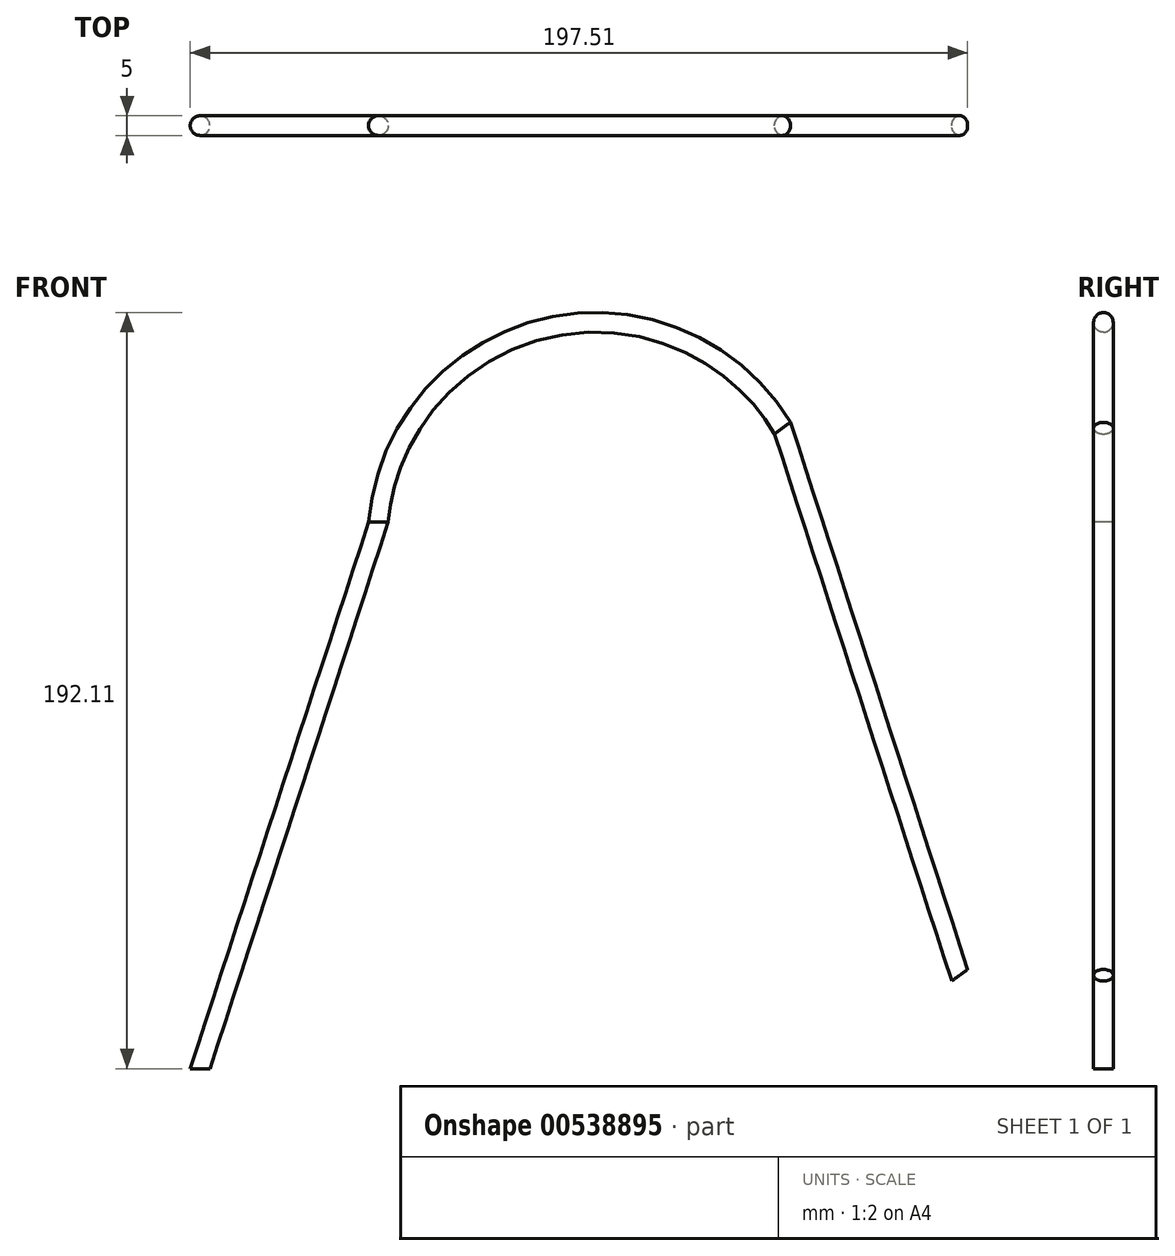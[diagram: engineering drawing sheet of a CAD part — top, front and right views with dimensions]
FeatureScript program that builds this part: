
annotation { "Feature Type Name" : "Feature", "Feature Type Description" : "" }
export const myFeature = defineFeature(function(context is Context, id is Id, definition is map)
    precondition{}
    {
        {
            var Q0;
            Q0=qCreatedBy(makeId("Front.planeOp"),FACE);
            var sketch = newSketch(context, id + "F0", { "sketchPlane" : qUnion([Q0])});
            skLineSegment(sketch, "E0", {"start": v(-60, 0) * mm, "end": v(-15, 137.84) * mm});
            skLineSegment(sketch, "E1", {"start": v(15, 139.03) * mm, "end": v(60, 0) * mm});
            skLineSegment(sketch, "E2", {"start": v(0, 0) * mm, "end": v(0, 168.43) * mm, "construction": true});
            skArc(sketch, "E3", {"start": v(15, 139.03) * mm, "mid": v(-0.45, 149.8) * mm, "end": v(-15, 137.84) * mm});
            skSolve(sketch);
        }
        {
            var Q0;
            Q0=qCreatedBy(makeId("Top.planeOp"),FACE);
            var sketch = newSketch(context, id + "F1", { "sketchPlane" : qUnion([Q0])});
            skCircle(sketch, "E4", {"center": v(-100.35, 0) * mm, "radius": 2.5 * mm});
            skSolve(sketch);
        }
        {
            var Q0;
            Q0=makeQuery(id+"F1.imprint","IMPRINT",FACE,{"disambiguationData":[TD([[makeQuery(id+"F1.imprint","IMPRINT",EDGE,{"derivedFrom":sQuery(id+"F1.wireOp",EDGE,"E4")}),1.0]])]});
            var Q1;
            Q1=sQuery(id+"F0.wireOp",EDGE,"E0");
            var Q2;
            Q2=sQuery(id+"F0.wireOp",EDGE,"E3");
            var Q3;
            Q3=sQuery(id+"F0.wireOp",EDGE,"E1");
            sweep(context, id + "F2", {"profiles" : qUnion([Q0]), "path" : qUnion([Q1, Q2, Q3])});
        }
    });
